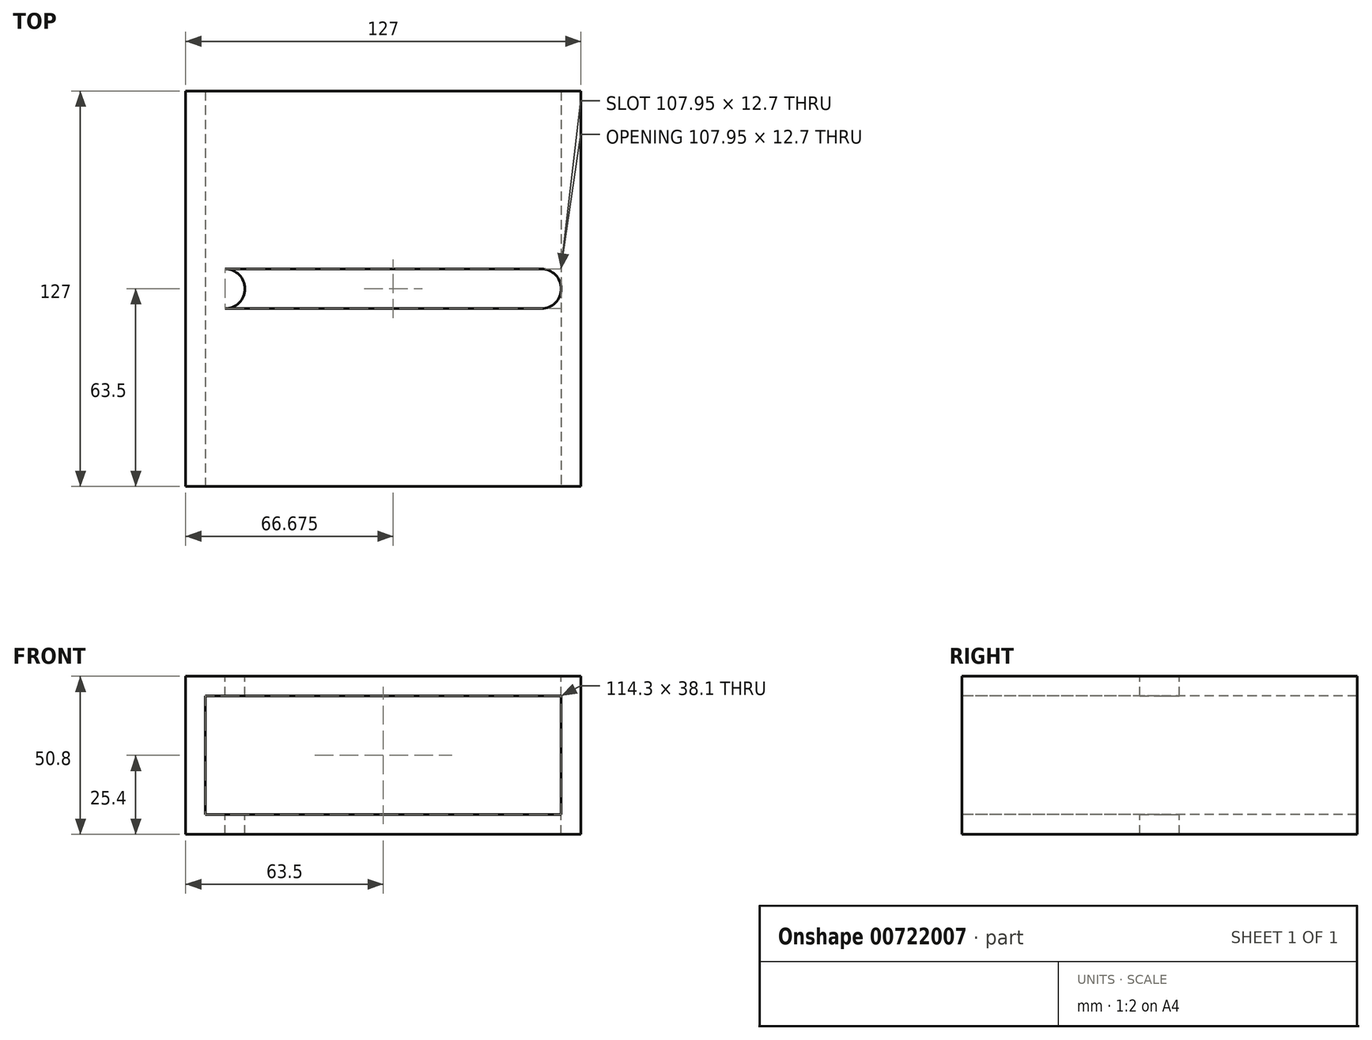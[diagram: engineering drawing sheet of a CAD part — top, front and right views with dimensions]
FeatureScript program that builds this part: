
annotation { "Feature Type Name" : "Feature", "Feature Type Description" : "" }
export const myFeature = defineFeature(function(context is Context, id is Id, definition is map)
    precondition{}
    {
        {
            var Q0;
            Q0=qCreatedBy(makeId("Top.planeOp"),FACE);
            var sketch = newSketch(context, id + "F0", { "sketchPlane" : qUnion([Q0])});
            skLineSegment(sketch, "E0.bottom", {"start": v(63.5, -63.5) * mm, "end": v(-63.5, -63.5) * mm});
            skLineSegment(sketch, "E0.top", {"start": v(63.5, 63.5) * mm, "end": v(-63.5, 63.5) * mm});
            skLineSegment(sketch, "E0.left", {"start": v(63.5, -63.5) * mm, "end": v(63.5, 63.5) * mm});
            skLineSegment(sketch, "E0.right", {"start": v(-63.5, -63.5) * mm, "end": v(-63.5, 63.5) * mm});
            skPoint(sketch, "E0.middle", {"position": v(0, 0) * mm});
            skSolve(sketch);
        }
        {
            var Q0;
            Q0=makeQuery(id+"F0.imprint","IMPRINT",FACE,{"disambiguationData":[TD([[makeQuery(id+"F0.imprint","IMPRINT",EDGE,{"derivedFrom":sQuery(id+"F0.wireOp",EDGE,"E0.bottom")}),-1.0]])]});
            extrude(context, id + "F1", {"entities" : qUnion([Q0]), "depth" : 50.8 * mm, "offsetDistance" : 25.4 * mm});
        }
        {
            var Q0;
            Q0=makeQuery(id+"F1.opExtrude","SWEPT_FACE",FACE,{"disambiguationData":[OSD([sQuery(id+"F0.wireOp",EDGE,"E0.bottom")])]});
            var sketch = newSketch(context, id + "F2", { "sketchPlane" : qUnion([Q0])});
            skLineSegment(sketch, "E1.0", {"start": v(-63.5, 50.8) * mm, "end": v(-63.5, 0) * mm});
            skLineSegment(sketch, "E2.0", {"start": v(63.5, 50.8) * mm, "end": v(-63.5, 50.8) * mm});
            skLineSegment(sketch, "E3.0", {"start": v(63.5, 50.8) * mm, "end": v(63.5, 0) * mm});
            skLineSegment(sketch, "E4.0", {"start": v(63.5, 0) * mm, "end": v(-63.5, 0) * mm});
            skLineSegment(sketch, "E5.0", {"start": v(-57.15, 44.45) * mm, "end": v(-57.15, 6.35) * mm});
            skLineSegment(sketch, "E5.1", {"start": v(57.15, 44.45) * mm, "end": v(-57.15, 44.45) * mm});
            skLineSegment(sketch, "E5.2", {"start": v(57.15, 44.45) * mm, "end": v(57.15, 6.35) * mm});
            skLineSegment(sketch, "E5.3", {"start": v(57.15, 6.35) * mm, "end": v(-57.15, 6.35) * mm});
            skSolve(sketch);
        }
        {
            var Q0;
            Q0=makeQuery(id+"F2.imprint","IMPRINT",FACE,{"disambiguationData":[TD([[makeQuery(id+"F2.imprint","IMPRINT",EDGE,{"derivedFrom":sQuery(id+"F2.wireOp",EDGE,"E5.0")}),1.0]])]});
            extrude(context, id + "F3", {"entities" : qUnion([Q0]), "operationType" : NewBodyOperationType.REMOVE, "endBound" : BoundingType.THROUGH_ALL, "oppositeDirection" : true, "depth" : 25.4 * mm, "offsetDistance" : 25.4 * mm});
        }
        {
            var Q0;
            Q0=makeQuery(id+"F1.opExtrude","CAP_FACE",FACE,{"disambiguationData":[OSD([sQuery(id+"F0.wireOp",EDGE,"E0.bottom"),sQuery(id+"F0.wireOp",EDGE,"E0.top"),sQuery(id+"F0.wireOp",EDGE,"E0.left"),sQuery(id+"F0.wireOp",EDGE,"E0.right")])],"isStart":false});
            var sketch = newSketch(context, id + "F4", { "sketchPlane" : qUnion([Q0])});
            skLineSegment(sketch, "E6", {"start": v(63.5, 0) * mm, "end": v(-63.5, 0) * mm, "construction": true});
            skLineSegment(sketch, "E7", {"start": v(0, 63.5) * mm, "end": v(0, -63.5) * mm, "construction": true});
            skCircle(sketch, "E8", {"center": v(50.8, 0) * mm, "radius": 6.35 * mm});
            skLineSegment(sketch, "E9.0", {"start": v(-57.15, 63.5) * mm, "end": v(-57.15, -63.5) * mm});
            skLineSegment(sketch, "E10.0", {"start": v(57.15, 63.5) * mm, "end": v(57.15, -63.5) * mm});
            skCircle(sketch, "E11.MirrorC", {"center": v(-50.8, 0) * mm, "radius": 6.35 * mm});
            skLineSegment(sketch, "E12", {"start": v(50.8, -6.35) * mm, "end": v(-50.8, -6.35) * mm});
            skLineSegment(sketch, "E13.MirrorCS", {"start": v(50.8, 6.35) * mm, "end": v(-50.8, 6.35) * mm});
            skSolve(sketch);
        }
        {
            var Q0;
            {var subQ0=sQuery(id+"F4.wireOp",EDGE,"E12");Q0=makeQuery(id+"F4.imprint","IMPRINT",FACE,{"disambiguationData":[TD([[makeQuery(id+"F4.imprint","IMPRINT",EDGE,{"derivedFrom":subQ0}),-1.0]])]});}
            var Q1;
            {var subQ0=sQuery(id+"F4.wireOp",EDGE,"E8");var subQ1=makeQuery(id+"F4.imprint","INTERSECT",VERTEX,{"derivedFrom":[subQ0,sQuery(id+"F4.wireOp",EDGE,"E13.MirrorCS")]});Q1=makeQuery(id+"F4.imprint","IMPRINT",FACE,{"disambiguationData":[TD([[makeQuery(id+"F4.imprint","IMPRINT",EDGE,{"disambiguationData":[TD([[subQ1,1.0]])],"derivedFrom":subQ0}),1.0]])]});}
            var Q2;
            {var subQ0=sQuery(id+"F4.wireOp",EDGE,"E11.MirrorC");var subQ1=makeQuery(id+"F4.imprint","INTERSECT",VERTEX,{"derivedFrom":[subQ0,sQuery(id+"F4.wireOp",EDGE,"E13.MirrorCS")]});Q2=makeQuery(id+"F4.imprint","IMPRINT",FACE,{"disambiguationData":[TD([[makeQuery(id+"F4.imprint","IMPRINT",EDGE,{"disambiguationData":[TD([[subQ1,1.0]])],"derivedFrom":subQ0}),-1.0]])]});}
            extrude(context, id + "F5", {"entities" : qUnion([Q0, Q1, Q2]), "operationType" : NewBodyOperationType.REMOVE, "endBound" : BoundingType.THROUGH_ALL, "oppositeDirection" : true, "depth" : 25.4 * mm, "offsetDistance" : 25.4 * mm});
        }
    });
